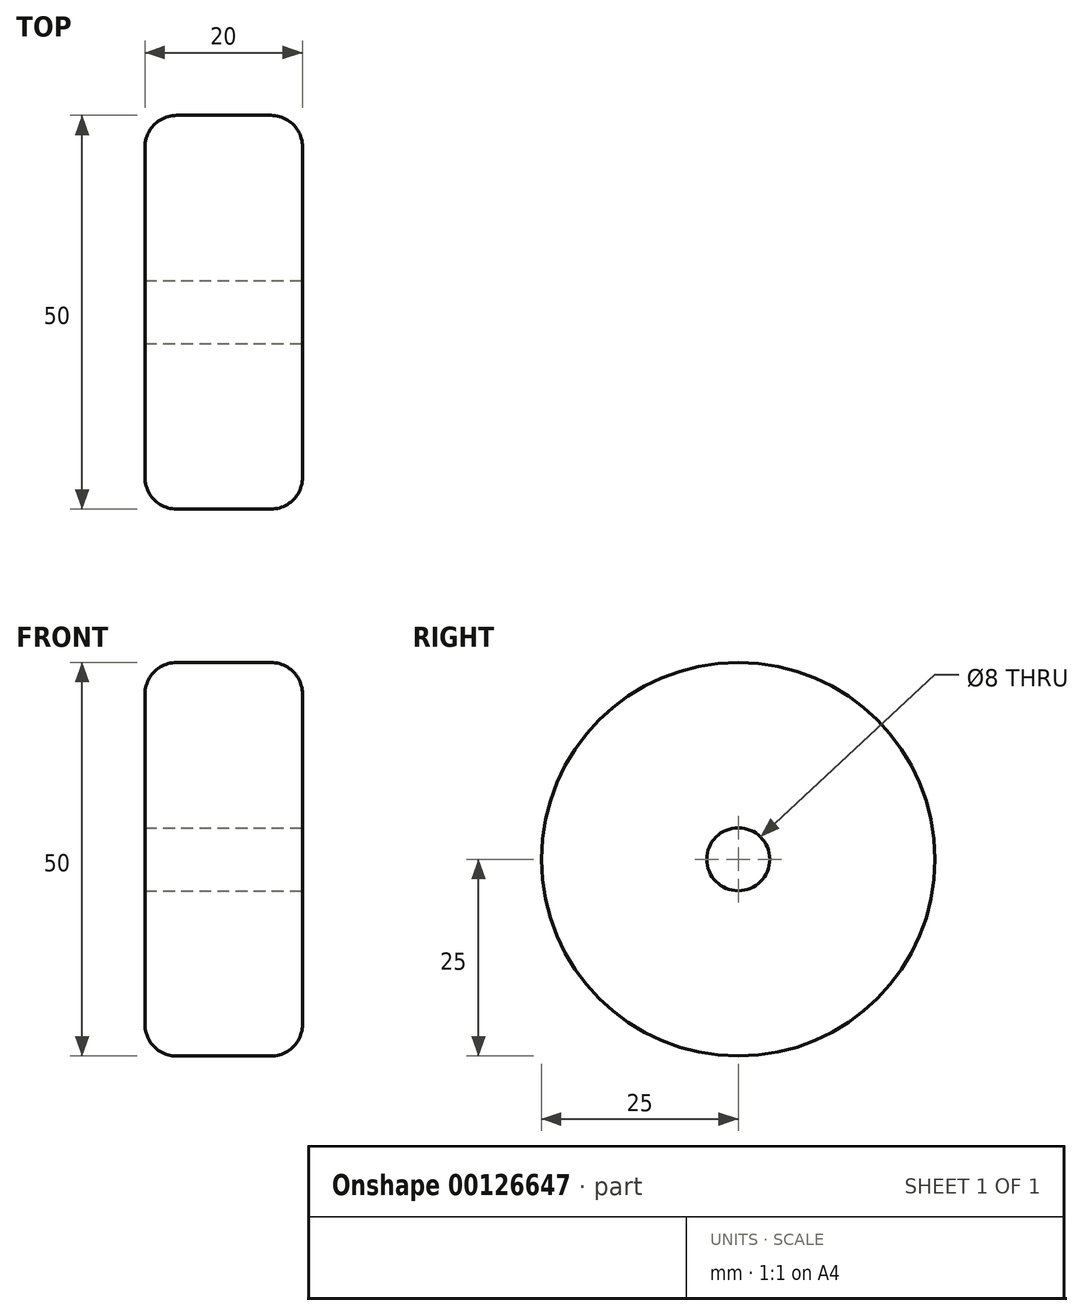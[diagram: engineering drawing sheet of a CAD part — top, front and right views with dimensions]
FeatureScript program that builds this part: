
annotation { "Feature Type Name" : "Feature", "Feature Type Description" : "" }
export const myFeature = defineFeature(function(context is Context, id is Id, definition is map)
    precondition{}
    {
        {
            var Q0;
            Q0=qCreatedBy(makeId("Top.planeOp"),FACE);
            var sketch = newSketch(context, id + "F0", { "sketchPlane" : qUnion([Q0])});
            skLineSegment(sketch, "E0", {"start": v(0, 0) * mm, "end": v(-20, 0) * mm});
            skLineSegment(sketch, "E1", {"start": v(-20, 0) * mm, "end": v(-20, 21) * mm});
            skLineSegment(sketch, "E2", {"start": v(-16, 25) * mm, "end": v(-4, 25) * mm});
            skLineSegment(sketch, "E3", {"start": v(0, 21) * mm, "end": v(0, 0) * mm});
            skLineSegment(sketch, "E4", {"start": v(0, 4) * mm, "end": v(-20, 4) * mm});
            skLineSegment(sketch, "E5.0", {"start": v(0, 19) * mm, "end": v(-20, 19) * mm});
            skPoint(sketch, "E6.visualSharp", {"position": v(-20, 25) * mm});
            skArc(sketch, "E6.filletArc", {"start": v(-16, 25) * mm, "mid": v(-18.83, 23.83) * mm, "end": v(-20, 21) * mm});
            skPoint(sketch, "E7.visualSharp", {"position": v(0, 25) * mm});
            skArc(sketch, "E7.filletArc", {"start": v(0, 21) * mm, "mid": v(-1.17, 23.83) * mm, "end": v(-4, 25) * mm});
            skSolve(sketch);
        }
        {
            var Q0;
            {var subQ0=sQuery(id+"F0.wireOp",EDGE,"E4");Q0=makeQuery(id+"F0.imprint","IMPRINT",FACE,{"disambiguationData":[TD([[makeQuery(id+"F0.imprint","IMPRINT",EDGE,{"derivedFrom":subQ0}),-1.0]])]});}
            var Q1;
            Q1=sQuery(id+"F0.wireOp",EDGE,"E0");
            revolve(context, id + "F1", {"entities" : qUnion([Q0]), "axis" : qUnion([Q1]), "revolveType" : RevolveType.FULL});
        }
        {
            var Q0;
            Q0=makeQuery(id+"F0.imprint","IMPRINT",FACE,{"disambiguationData":[TD([[makeQuery(id+"F0.imprint","IMPRINT",EDGE,{"derivedFrom":sQuery(id+"F0.wireOp",EDGE,"E2")}),-1.0]])]});
            var Q1;
            Q1=sQuery(id+"F0.wireOp",EDGE,"E0");
            revolve(context, id + "F2", {"operationType" : NewBodyOperationType.ADD, "entities" : qUnion([Q0]), "axis" : qUnion([Q1]), "revolveType" : RevolveType.FULL});
        }
    });
